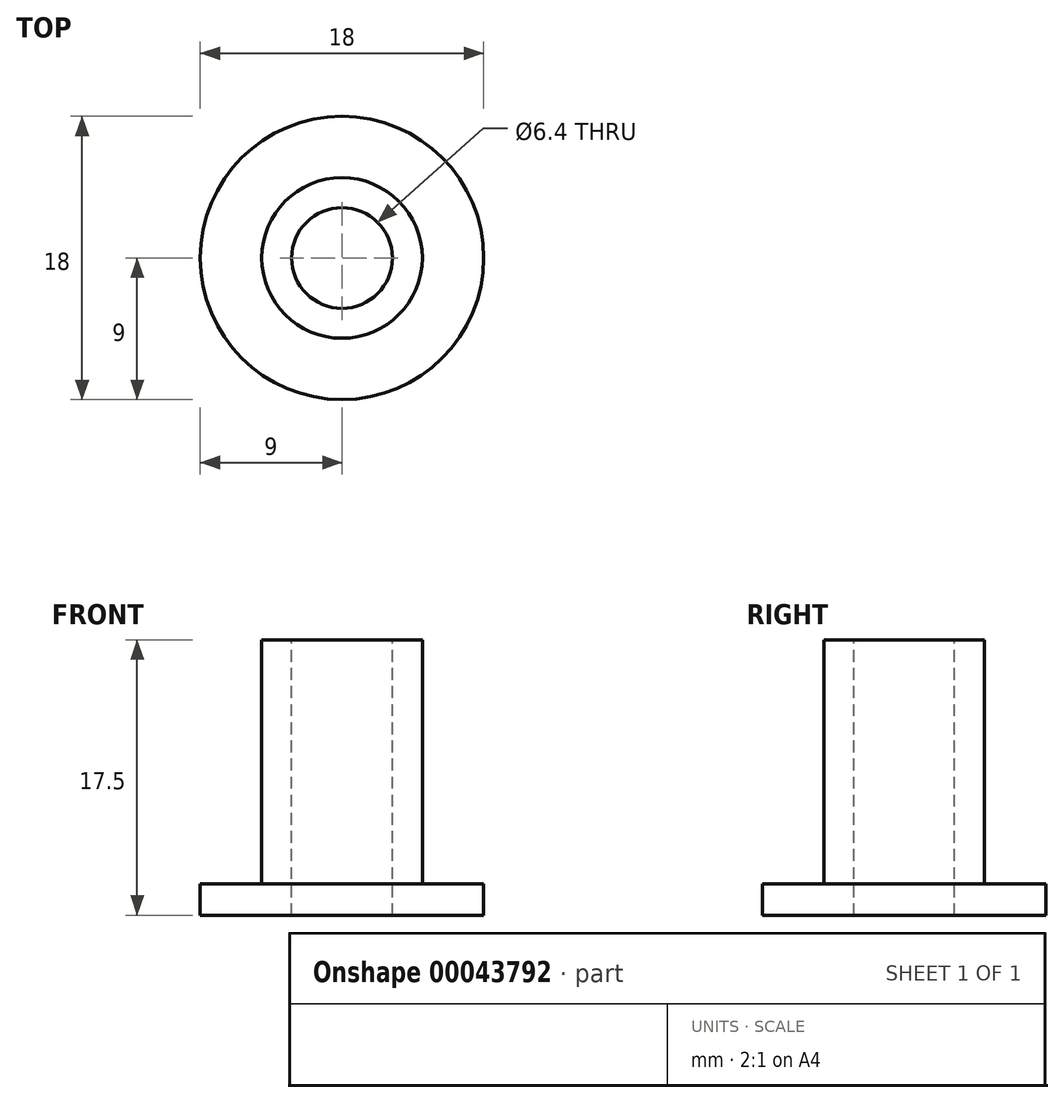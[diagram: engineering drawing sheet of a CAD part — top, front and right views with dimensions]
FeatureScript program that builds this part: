
annotation { "Feature Type Name" : "Feature", "Feature Type Description" : "" }
export const myFeature = defineFeature(function(context is Context, id is Id, definition is map)
    precondition{}
    {
        {
            var Q0;
            Q0=qCreatedBy(makeId("Front.planeOp"),FACE);
            var sketch = newSketch(context, id + "F0", { "sketchPlane" : qUnion([Q0])});
            skLineSegment(sketch, "E0", {"start": v(-9, 0) * mm, "end": v(-9, 2) * mm});
            skLineSegment(sketch, "E1", {"start": v(-9, 2) * mm, "end": v(-5.1, 2) * mm});
            skLineSegment(sketch, "E2", {"start": v(-9, 0) * mm, "end": v(-3.2, 0) * mm});
            skLineSegment(sketch, "E3", {"start": v(-3.2, 0) * mm, "end": v(-3.2, 17.5) * mm});
            skLineSegment(sketch, "E4", {"start": v(-3.2, 17.5) * mm, "end": v(-5.1, 17.5) * mm});
            skLineSegment(sketch, "E5", {"start": v(-5.1, 17.5) * mm, "end": v(-5.1, 2) * mm});
            skLineSegment(sketch, "E6", {"start": v(0, 23.67) * mm, "end": v(0, -2.1) * mm});
            skSolve(sketch);
        }
        {
            var Q0;
            Q0 = qSketchRegion(id + "F0", true);
            var Q1;
            Q1=sQuery(id+"F0.wireOp",EDGE,"E6");
            revolve(context, id + "F1", {"entities" : qUnion([Q0]), "axis" : qUnion([Q1]), "revolveType" : RevolveType.FULL});
        }
    });
